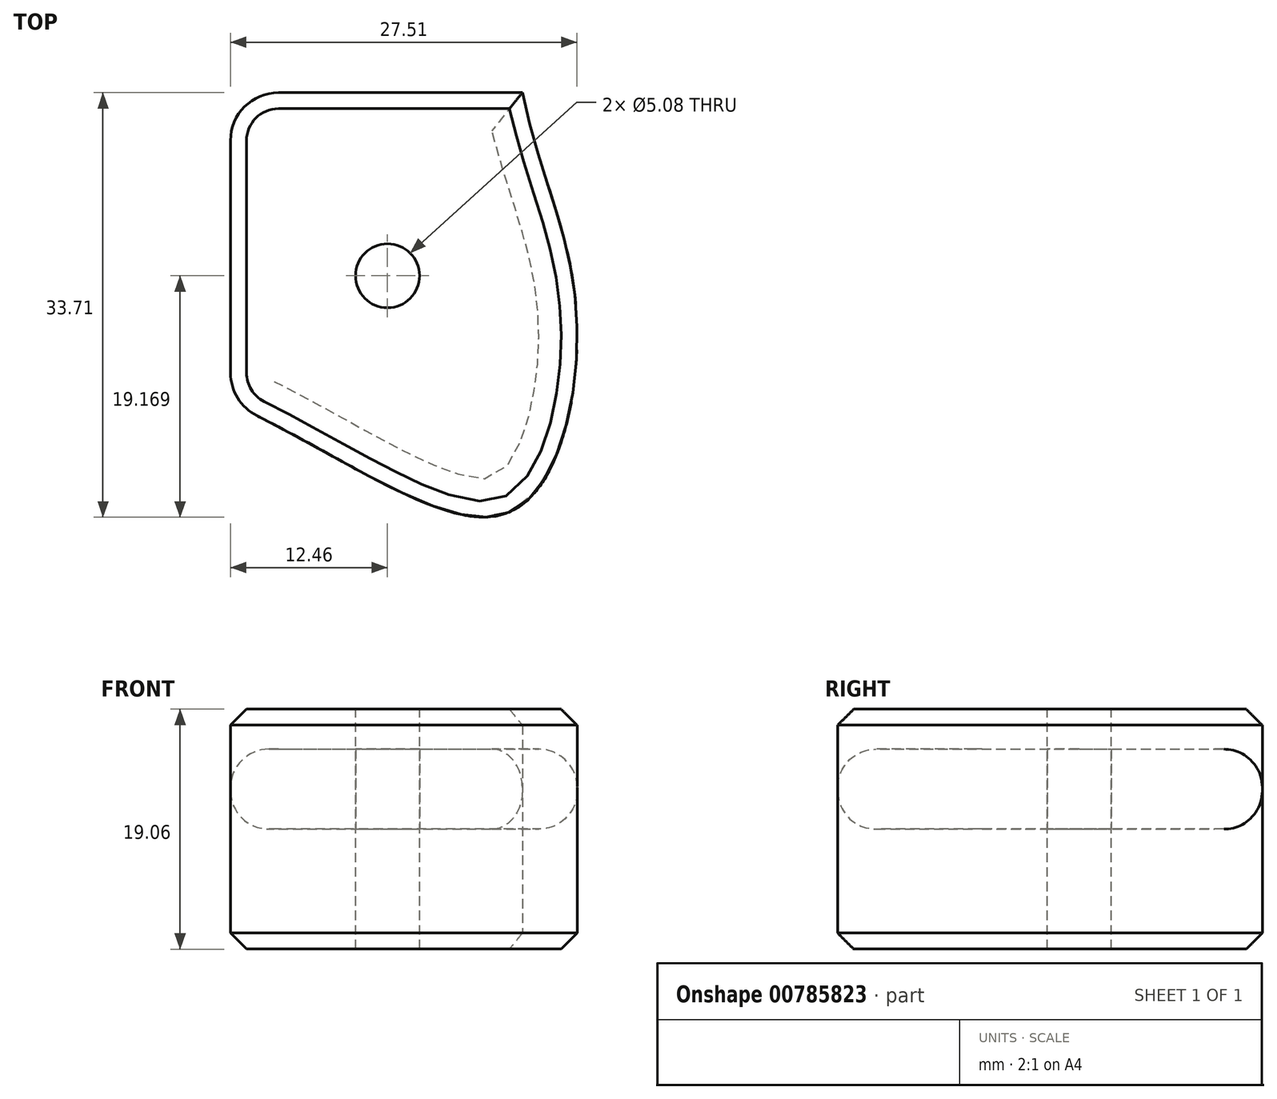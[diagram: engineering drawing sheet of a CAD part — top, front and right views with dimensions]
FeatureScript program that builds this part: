
annotation { "Feature Type Name" : "Feature", "Feature Type Description" : "" }
export const myFeature = defineFeature(function(context is Context, id is Id, definition is map)
    precondition{}
    {
        {
            var Q0;
            Q0=qCreatedBy(makeId("Top.planeOp"),FACE);
            var sketch = newSketch(context, id + "F0", { "sketchPlane" : qUnion([Q0])});
            skFitSpline(sketch, "E0", {"points": [v(0, 0) * mm, v(0, 28.92) * mm, v(9.35, 59.8) * mm, v(31.1, 65.45) * mm, v(43.7, 50.23) * mm, v(41.1, 30.22) * mm, v(35, 31.1) * mm, v(36.31, 40.23) * mm, v(30.22, 54.58) * mm, v(15.44, 50.66) * mm, v(9.78, 30.66) * mm, v(10.7, 0) * mm, v(15, -17.61) * mm, v(9.78, -33.27) * mm, v(-12.46, -24.64) * mm], "startDerivative": vector(0, 315.59) * mm, "endDerivative": vector(-356.12, 166.28) * mm});
            skLineSegment(sketch, "E1", {"start": v(-12.46, -22.26) * mm, "end": v(-12.46, -3.81) * mm});
            skPoint(sketch, "E2.visualSharp", {"position": v(-12.46, 0) * mm});
            skArc(sketch, "E2.filletArc", {"start": v(-8.65, 0) * mm, "mid": v(-11.35, -1.12) * mm, "end": v(-12.46, -3.81) * mm});
            skArc(sketch, "E3.filletArc", {"start": v(-12.46, -22.26) * mm, "mid": v(-11.9, -24.25) * mm, "end": v(-10.37, -25.66) * mm});
            skLineSegment(sketch, "E4", {"start": v(-8.65, 0) * mm, "end": v(10.7, 0) * mm});
            skSolve(sketch);
        }
        {
            var Q0;
            {var subQ0=sQuery(id+"F0.wireOp",EDGE,"E4");var subQ1=sQuery(id+"F0.wireOp",EDGE,"E0");var subQ2=makeQuery(id+"F0.imprint","INTERSECT",VERTEX,{"disambiguationData":[OD(0.0)],"derivedFrom":[subQ1,subQ0]});Q0=makeQuery(id+"F0.imprint","IMPRINT",FACE,{"disambiguationData":[TD([[makeQuery(id+"F0.imprint","IMPRINT",EDGE,{"disambiguationData":[TD([[subQ2,-1.0]])],"derivedFrom":subQ1}),-1.0]])]});}
            extrude(context, id + "F1", {"entities" : qUnion([Q0]), "depth" : 6.35 * mm, "offsetDistance" : 25.4 * mm});
        }
        {
            var Q0;
            Q0=makeQuery(id+"F1.opExtrude","CAP_EDGE",EDGE,{"disambiguationData":[OSD([sQuery(id+"F0.wireOp",EDGE,"E0")])],"isStart":false});
            var Q1;
            Q1=makeQuery(id+"F1.opExtrude","CAP_EDGE",EDGE,{"disambiguationData":[OSD([sQuery(id+"F0.wireOp",EDGE,"E0")])],"isStart":true});
            fillet(context, id + "F2", {"entities" : qUnion([Q0, Q1]), "radius" : 3.05 * mm, "tangentPropagation" : true, "allowEdgeOverflow" : false});
        }
        {
            var Q0;
            Q0=makeQuery(id+"F0.imprint","IMPRINT",FACE,{"disambiguationData":[TD([[makeQuery(id+"F0.imprint","IMPRINT",EDGE,{"derivedFrom":sQuery(id+"F0.wireOp",EDGE,"E1")}),-1.0]])]});
            extrude(context, id + "F3", {"entities" : qUnion([Q0]), "endBound" : BoundingType.SYMMETRIC, "depth" : 19.05 * mm, "offsetDistance" : 25.4 * mm});
        }
        {
            var Q0;
            Q0=makeQuery(id+"F3.opExtrude","CAP_EDGE",EDGE,{"disambiguationData":[OSD([sQuery(id+"F0.wireOp",EDGE,"E0")])],"isStart":false});
            var Q1;
            Q1=makeQuery(id+"F3.opExtrude","CAP_EDGE",EDGE,{"disambiguationData":[OSD([sQuery(id+"F0.wireOp",EDGE,"E1")])],"isStart":false});
            var Q2;
            Q2=makeQuery(id+"F3.opExtrude","CAP_EDGE",EDGE,{"disambiguationData":[OSD([sQuery(id+"F0.wireOp",EDGE,"E0")])],"isStart":true});
            var Q3;
            Q3=makeQuery(id+"F3.opExtrude","CAP_EDGE",EDGE,{"disambiguationData":[OSD([sQuery(id+"F0.wireOp",EDGE,"E1")])],"isStart":true});
            var Q4;
            Q4=makeQuery(id+"F3.opExtrude","CAP_EDGE",EDGE,{"disambiguationData":[OSD([sQuery(id+"F0.wireOp",EDGE,"1eBXH4wU-6Gse-WPX3-7sSV-rDY6sM5wLBnP"),sQuery(id+"F0.wireOp",EDGE,"JdfsQdGy-6Jv0-wgyS-EMNI-XhSbFJdsthdE")])],"isStart":true});
            chamfer(context, id + "F4", {"entities" : qUnion([Q0, Q1, Q2, Q3, Q4]), "width" : 1.27 * mm, "tangentPropagation" : true});
        }
        {
            var Q0;
            Q0=qCreatedBy(makeId("Top.planeOp"),FACE);
            var sketch = newSketch(context, id + "F5", { "sketchPlane" : qUnion([Q0])});
            skCircle(sketch, "E5", {"center": v(0, -14.54) * mm, "radius": 2.54 * mm});
            skSolve(sketch);
        }
        {
            var Q0;
            Q0=sQuery(id+"F5.wireOp",VERTEX,"E5.center");
            var Q1;
            Q1=makeQuery(id+"F3.opExtrude","SWEPT_BODY",BODY,{"disambiguationData":[OSD([sQuery(id+"F0.wireOp",EDGE,"E0"),sQuery(id+"F0.wireOp",EDGE,"E1"),sQuery(id+"F0.wireOp",EDGE,"1eBXH4wU-6Gse-WPX3-7sSV-rDY6sM5wLBnP"),sQuery(id+"F0.wireOp",EDGE,"E2.filletArc"),sQuery(id+"F0.wireOp",EDGE,"E3.filletArc"),sQuery(id+"F0.wireOp",EDGE,"JdfsQdGy-6Jv0-wgyS-EMNI-XhSbFJdsthdE")])]});
            hole(context, id + "F6", {"style" : HoleStyle.SIMPLE, "endStyle" : HoleEndStyle.BLIND, "holeDiameter" : 5.08 * mm, "majorDiameter" : 6.35 * mm, "holeDepth" : 2540 * mm, "isTappedThrough" : true, "tappedDepth" : 12.7 * mm, "tapClearance" : 3, "locations" : qUnion([Q0]), "scope" : qUnion([Q1])});
        }
        {
            var Q0;
            Q0=sQuery(id+"F5.wireOp",VERTEX,"E5.center");
            var Q1;
            Q1=makeQuery(id+"F1.opExtrude","SWEPT_BODY",BODY,{"disambiguationData":[OSD([sQuery(id+"F0.wireOp",EDGE,"E0"),sQuery(id+"F0.wireOp",EDGE,"E1"),sQuery(id+"F0.wireOp",EDGE,"1eBXH4wU-6Gse-WPX3-7sSV-rDY6sM5wLBnP"),sQuery(id+"F0.wireOp",EDGE,"E2.filletArc"),sQuery(id+"F0.wireOp",EDGE,"E3.filletArc")])]});
            var Q2;
            Q2=makeQuery(id+"F3.opExtrude","SWEPT_BODY",BODY,{"disambiguationData":[OSD([sQuery(id+"F0.wireOp",EDGE,"E0"),sQuery(id+"F0.wireOp",EDGE,"E1"),sQuery(id+"F0.wireOp",EDGE,"1eBXH4wU-6Gse-WPX3-7sSV-rDY6sM5wLBnP"),sQuery(id+"F0.wireOp",EDGE,"E2.filletArc"),sQuery(id+"F0.wireOp",EDGE,"E3.filletArc"),sQuery(id+"F0.wireOp",EDGE,"JdfsQdGy-6Jv0-wgyS-EMNI-XhSbFJdsthdE")])]});
            hole(context, id + "F7", {"style" : HoleStyle.SIMPLE, "endStyle" : HoleEndStyle.BLIND, "oppositeDirection" : true, "holeDiameter" : 5.08 * mm, "majorDiameter" : 6.35 * mm, "holeDepth" : 2540 * mm, "isTappedThrough" : true, "tappedDepth" : 12.7 * mm, "tapClearance" : 3, "locations" : qUnion([Q0]), "scope" : qUnion([Q1, Q2])});
        }
    });
